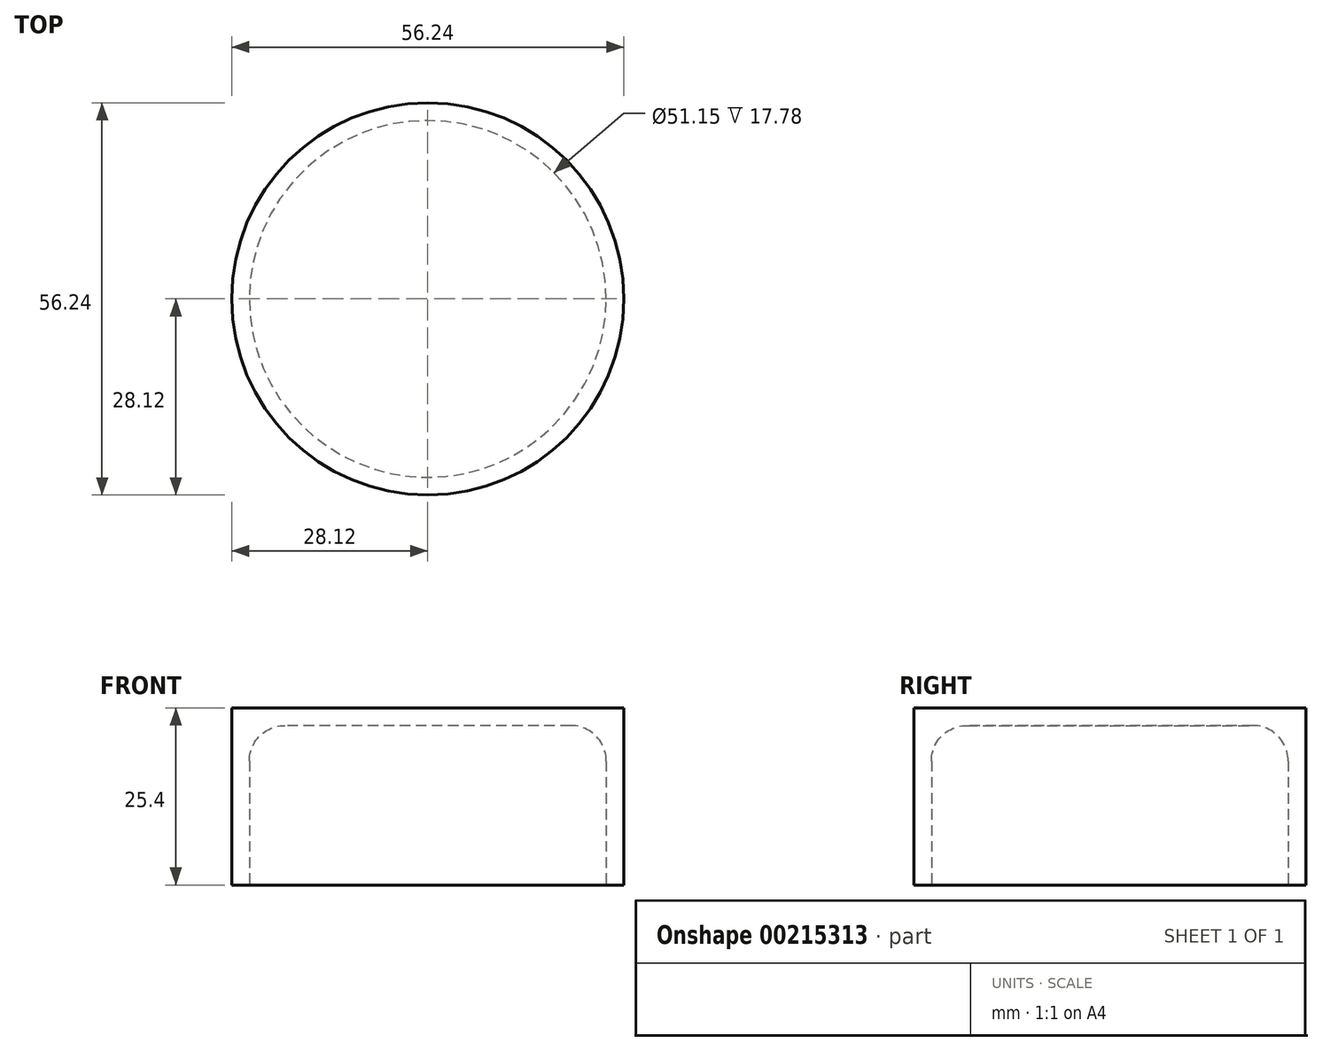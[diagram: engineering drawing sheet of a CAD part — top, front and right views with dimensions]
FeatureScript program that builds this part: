
annotation { "Feature Type Name" : "Feature", "Feature Type Description" : "" }
export const myFeature = defineFeature(function(context is Context, id is Id, definition is map)
    precondition{}
    {
        {
            var Q0;
            Q0=qCreatedBy(makeId("Top.planeOp"),FACE);
            var sketch = newSketch(context, id + "F0", { "sketchPlane" : qUnion([Q0])});
            skCircle(sketch, "E0", {"center": v(0, 0) * mm, "radius": 28.12 * mm});
            skSolve(sketch);
        }
        {
            var Q0;
            Q0=makeQuery(id+"F0.imprint","IMPRINT",FACE,{"disambiguationData":[TD([[makeQuery(id+"F0.imprint","IMPRINT",EDGE,{"derivedFrom":sQuery(id+"F0.wireOp",EDGE,"E0")}),1.0]])]});
            extrude(context, id + "F1", {"entities" : qUnion([Q0]), "depth" : 25.4 * mm});
        }
        {
            var Q0;
            Q0=makeQuery(id+"F1.opExtrude","CAP_FACE",FACE,{"disambiguationData":[OSD([sQuery(id+"F0.wireOp",EDGE,"E0")])],"isStart":true});
            shell(context, id + "F2", {"entities" : qUnion([Q0]), "thickness" : 2.54 * mm});
        }
        {
            var Q0;
            {var subQ0=sQuery(id+"F0.wireOp",EDGE,"E0");Q0=makeQuery(id+"F2.opShell","OFFSET_FACE",FACE,{"disambiguationData":[OSD([subQ0]),TDD([makeQuery(id+"F1.opExtrude","CAP_FACE",FACE,{"disambiguationData":[OSD([subQ0])],"isStart":false})])]});}
            fillet(context, id + "F3", {"entities" : qUnion([Q0]), "radius" : 5.08 * mm, "tangentPropagation" : true, "allowEdgeOverflow" : false});
        }
    });
